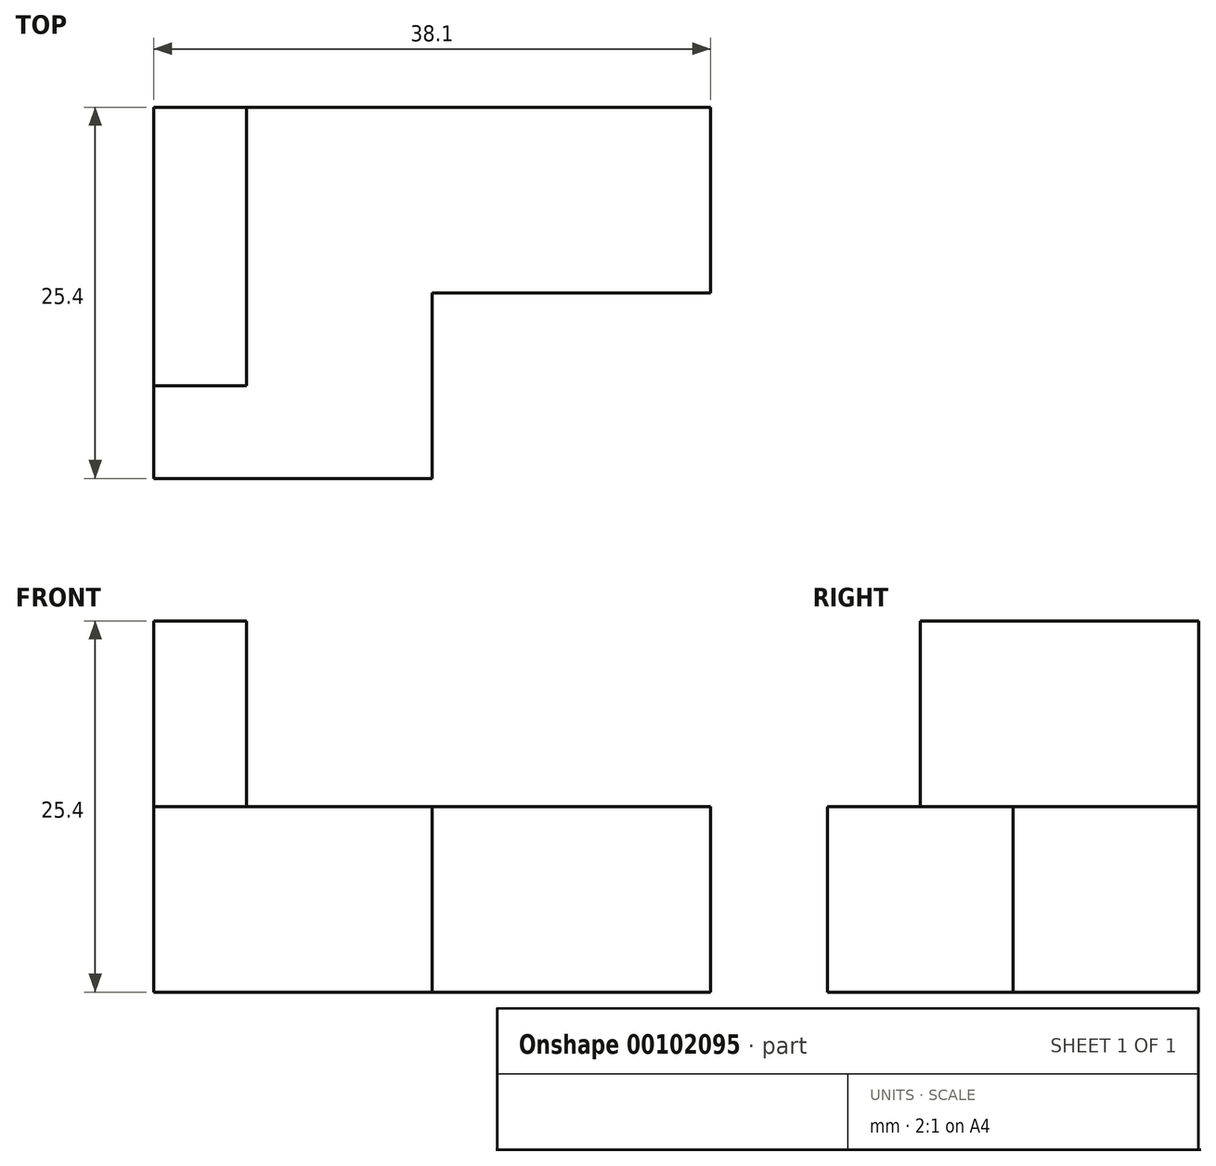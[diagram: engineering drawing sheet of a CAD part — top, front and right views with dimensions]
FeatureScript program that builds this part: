
annotation { "Feature Type Name" : "Feature", "Feature Type Description" : "" }
export const myFeature = defineFeature(function(context is Context, id is Id, definition is map)
    precondition{}
    {
        {
            var Q0;
            Q0=qCreatedBy(makeId("Top.planeOp"),FACE);
            var sketch = newSketch(context, id + "F0", { "sketchPlane" : qUnion([Q0])});
            skLineSegment(sketch, "E0", {"start": v(0, 0) * mm, "end": v(19.05, 0) * mm});
            skLineSegment(sketch, "E1", {"start": v(19.05, 0) * mm, "end": v(19.05, 12.7) * mm});
            skLineSegment(sketch, "E2", {"start": v(19.05, 12.7) * mm, "end": v(38.1, 12.7) * mm});
            skLineSegment(sketch, "E3", {"start": v(38.1, 12.7) * mm, "end": v(38.1, 25.4) * mm});
            skLineSegment(sketch, "E4", {"start": v(38.1, 25.4) * mm, "end": v(0, 25.4) * mm});
            skLineSegment(sketch, "E5", {"start": v(0, 25.4) * mm, "end": v(0, 0) * mm});
            skSolve(sketch);
        }
        {
            var Q0;
            Q0=makeQuery(id+"F0.imprint","IMPRINT",FACE,{"disambiguationData":[TD([[makeQuery(id+"F0.imprint","IMPRINT",EDGE,{"derivedFrom":sQuery(id+"F0.wireOp",EDGE,"E0")}),1.0]])]});
            extrude(context, id + "F1", {"entities" : qUnion([Q0]), "depth" : 12.7 * mm});
        }
        {
            var Q0;
            Q0=makeQuery(id+"F1.opExtrude","CAP_FACE",FACE,{"disambiguationData":[OSD([sQuery(id+"F0.wireOp",EDGE,"E0"),sQuery(id+"F0.wireOp",EDGE,"E1"),sQuery(id+"F0.wireOp",EDGE,"E2"),sQuery(id+"F0.wireOp",EDGE,"E3"),sQuery(id+"F0.wireOp",EDGE,"E4"),sQuery(id+"F0.wireOp",EDGE,"E5")])],"isStart":false});
            var sketch = newSketch(context, id + "F2", { "sketchPlane" : qUnion([Q0])});
            skLineSegment(sketch, "E6.bottom", {"start": v(0, 25.4) * mm, "end": v(6.35, 25.4) * mm});
            skLineSegment(sketch, "E6.top", {"start": v(0, 6.35) * mm, "end": v(6.35, 6.35) * mm});
            skLineSegment(sketch, "E6.left", {"start": v(0, 25.4) * mm, "end": v(0, 6.35) * mm});
            skLineSegment(sketch, "E6.right", {"start": v(6.35, 25.4) * mm, "end": v(6.35, 6.35) * mm});
            skSolve(sketch);
        }
        {
            var Q0;
            Q0=makeQuery(id+"F2.imprint","IMPRINT",FACE,{"disambiguationData":[TD([[makeQuery(id+"F2.imprint","IMPRINT",EDGE,{"derivedFrom":sQuery(id+"F2.wireOp",EDGE,"E6.bottom")}),1.0]])]});
            extrude(context, id + "F3", {"entities" : qUnion([Q0]), "operationType" : NewBodyOperationType.ADD, "depth" : 12.7 * mm});
        }
    });
